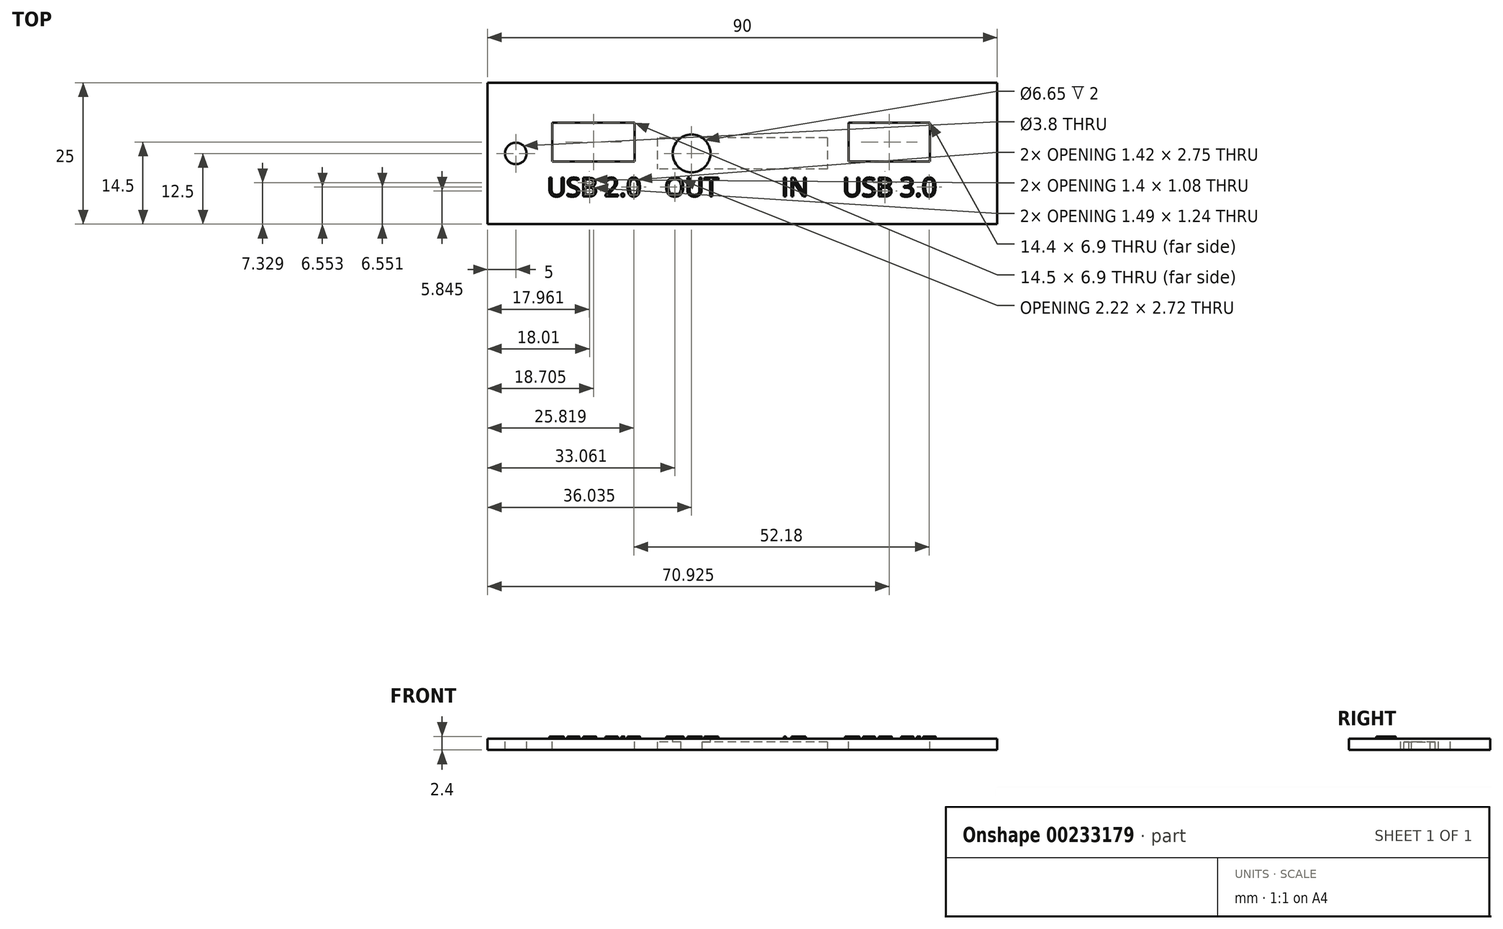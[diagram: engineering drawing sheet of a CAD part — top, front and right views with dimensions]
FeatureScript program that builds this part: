
annotation { "Feature Type Name" : "Feature", "Feature Type Description" : "" }
export const myFeature = defineFeature(function(context is Context, id is Id, definition is map)
    precondition{}
    {
        {
            var Q0;
            Q0=qCreatedBy(makeId("Top.planeOp"),FACE);
            var sketch = newSketch(context, id + "F0", { "sketchPlane" : qUnion([Q0])});
            skLineSegment(sketch, "E0.bottom", {"start": v(45, -12.5) * mm, "end": v(-45, -12.5) * mm});
            skLineSegment(sketch, "E0.top", {"start": v(45, 12.5) * mm, "end": v(-45, 12.5) * mm});
            skLineSegment(sketch, "E0.left", {"start": v(45, -12.5) * mm, "end": v(45, 12.5) * mm});
            skLineSegment(sketch, "E0.right", {"start": v(-45, -12.5) * mm, "end": v(-45, 12.5) * mm});
            skPoint(sketch, "E0.middle", {"position": v(0, 0) * mm});
            skSolve(sketch);
        }
        {
            var Q0;
            Q0=makeQuery(id+"F0.imprint","IMPRINT",FACE,{"disambiguationData":[TD([[makeQuery(id+"F0.imprint","IMPRINT",EDGE,{"derivedFrom":sQuery(id+"F0.wireOp",EDGE,"E0.bottom")}),-1.0]])]});
            extrude(context, id + "F1", {"entities" : qUnion([Q0]), "depth" : 2 * mm});
        }
        {
            var Q0;
            Q0=makeQuery(id+"F1.opExtrude","CAP_FACE",FACE,{"disambiguationData":[OSD([sQuery(id+"F0.wireOp",EDGE,"E0.bottom"),sQuery(id+"F0.wireOp",EDGE,"E0.top"),sQuery(id+"F0.wireOp",EDGE,"E0.left"),sQuery(id+"F0.wireOp",EDGE,"E0.right")])],"isStart":false});
            var sketch = newSketch(context, id + "F2", { "sketchPlane" : qUnion([Q0])});
            skCircle(sketch, "E1", {"center": v(-8.96, 0) * mm, "radius": 3.33 * mm});
            skSolve(sketch);
        }
        {
            var Q0;
            Q0=makeQuery(id+"F2.imprint","IMPRINT",FACE,{"disambiguationData":[TD([[makeQuery(id+"F2.imprint","IMPRINT",EDGE,{"derivedFrom":sQuery(id+"F2.wireOp",EDGE,"E1")}),1.0]])]});
            extrude(context, id + "F3", {"entities" : qUnion([Q0]), "operationType" : NewBodyOperationType.REMOVE, "endBound" : BoundingType.THROUGH_ALL, "oppositeDirection" : true, "depth" : 25.4 * mm});
        }
        {
            var Q0;
            Q0=makeQuery(id+"F1.opExtrude","CAP_FACE",FACE,{"disambiguationData":[OSD([sQuery(id+"F0.wireOp",EDGE,"E0.bottom"),sQuery(id+"F0.wireOp",EDGE,"E0.top"),sQuery(id+"F0.wireOp",EDGE,"E0.left"),sQuery(id+"F0.wireOp",EDGE,"E0.right")])],"isStart":false});
            var sketch = newSketch(context, id + "F4", { "sketchPlane" : qUnion([Q0])});
            skLineSegment(sketch, "E2.bottom", {"start": v(33.12, -1.45) * mm, "end": v(18.73, -1.45) * mm});
            skLineSegment(sketch, "E2.top", {"start": v(33.12, 5.45) * mm, "end": v(18.73, 5.45) * mm});
            skLineSegment(sketch, "E2.left", {"start": v(33.12, -1.45) * mm, "end": v(33.12, 5.45) * mm});
            skLineSegment(sketch, "E2.right", {"start": v(18.73, -1.45) * mm, "end": v(18.73, 5.45) * mm});
            skPoint(sketch, "E2.middle", {"position": v(25.93, 2) * mm});
            skPoint(sketch, "E3", {"position": v(8.96, 0) * mm});
            skSolve(sketch);
        }
        {
            var Q0;
            Q0=makeQuery(id+"F4.imprint","IMPRINT",FACE,{"disambiguationData":[TD([[makeQuery(id+"F4.imprint","IMPRINT",EDGE,{"derivedFrom":sQuery(id+"F4.wireOp",EDGE,"E2.bottom")}),-1.0]])]});
            extrude(context, id + "F5", {"entities" : qUnion([Q0]), "operationType" : NewBodyOperationType.REMOVE, "endBound" : BoundingType.THROUGH_ALL, "oppositeDirection" : true, "depth" : 25.4 * mm});
        }
        {
            var Q0;
            Q0=makeQuery(id+"F1.opExtrude","CAP_FACE",FACE,{"disambiguationData":[OSD([sQuery(id+"F0.wireOp",EDGE,"E0.bottom"),sQuery(id+"F0.wireOp",EDGE,"E0.top"),sQuery(id+"F0.wireOp",EDGE,"E0.left"),sQuery(id+"F0.wireOp",EDGE,"E0.right")])],"isStart":false});
            var sketch = newSketch(context, id + "F6", { "sketchPlane" : qUnion([Q0])});
            skLineSegment(sketch, "E4.bottom", {"start": v(-19.04, -1.45) * mm, "end": v(-33.55, -1.45) * mm});
            skLineSegment(sketch, "E4.top", {"start": v(-19.04, 5.45) * mm, "end": v(-33.55, 5.45) * mm});
            skLineSegment(sketch, "E4.left", {"start": v(-19.04, -1.45) * mm, "end": v(-19.04, 5.45) * mm});
            skLineSegment(sketch, "E4.right", {"start": v(-33.55, -1.45) * mm, "end": v(-33.55, 5.45) * mm});
            skPoint(sketch, "E4.middle", {"position": v(-26.3, 2) * mm});
            skPoint(sketch, "E5", {"position": v(-8.96, 0) * mm});
            skLineSegment(sketch, "E6.bottom", {"start": v(15, 2.75) * mm, "end": v(-15, 2.75) * mm});
            skLineSegment(sketch, "E6.top", {"start": v(15, -2.75) * mm, "end": v(-15, -2.75) * mm});
            skLineSegment(sketch, "E6.left", {"start": v(15, 2.75) * mm, "end": v(15, -2.75) * mm});
            skLineSegment(sketch, "E6.right", {"start": v(-15, 2.75) * mm, "end": v(-15, -2.75) * mm});
            skPoint(sketch, "E6.middle", {"position": v(0, 0) * mm});
            skSolve(sketch);
        }
        {
            var Q0;
            Q0=makeQuery(id+"F6.imprint","IMPRINT",FACE,{"disambiguationData":[TD([[makeQuery(id+"F6.imprint","IMPRINT",EDGE,{"derivedFrom":sQuery(id+"F6.wireOp",EDGE,"E4.bottom")}),-1.0]])]});
            extrude(context, id + "F7", {"entities" : qUnion([Q0]), "operationType" : NewBodyOperationType.REMOVE, "endBound" : BoundingType.THROUGH_ALL, "oppositeDirection" : true, "depth" : 25.4 * mm});
        }
        {
            var Q0;
            Q0=makeQuery(id+"F1.opExtrude","CAP_FACE",FACE,{"disambiguationData":[OSD([sQuery(id+"F0.wireOp",EDGE,"E0.bottom"),sQuery(id+"F0.wireOp",EDGE,"E0.top"),sQuery(id+"F0.wireOp",EDGE,"E0.left"),sQuery(id+"F0.wireOp",EDGE,"E0.right")])],"isStart":false});
            var sketch = newSketch(context, id + "F8", { "sketchPlane" : qUnion([Q0])});
            skLineSegment(sketch, "E7.0", {"start": v(-18.04, 6.45) * mm, "end": v(-34.55, 6.45) * mm});
            skLineSegment(sketch, "E7.1", {"start": v(-18.05, -2.45) * mm, "end": v(-18.04, 6.45) * mm});
            skLineSegment(sketch, "E7.2", {"start": v(-18.05, -2.45) * mm, "end": v(-34.55, -2.45) * mm});
            skLineSegment(sketch, "E7.3", {"start": v(-34.55, -2.45) * mm, "end": v(-34.55, 6.45) * mm});
            skLineSegment(sketch, "E8.0", {"start": v(51.35, -18.85) * mm, "end": v(51.35, 18.85) * mm});
            skLineSegment(sketch, "E8.1", {"start": v(-51.35, -18.85) * mm, "end": v(51.35, -18.85) * mm});
            skLineSegment(sketch, "E8.2", {"start": v(-51.35, 18.85) * mm, "end": v(-51.35, -18.85) * mm});
            skLineSegment(sketch, "E8.3", {"start": v(51.35, 18.85) * mm, "end": v(-51.35, 18.85) * mm});
            skSolve(sketch);
        }
        {
            var Q0;
            Q0=makeQuery(id+"F1.opExtrude","CAP_FACE",FACE,{"disambiguationData":[OSD([sQuery(id+"F0.wireOp",EDGE,"E0.bottom"),sQuery(id+"F0.wireOp",EDGE,"E0.top"),sQuery(id+"F0.wireOp",EDGE,"E0.left"),sQuery(id+"F0.wireOp",EDGE,"E0.right")])],"isStart":false});
            var sketch = newSketch(context, id + "F9", { "sketchPlane" : qUnion([Q0])});
            skLineSegment(sketch, "E9.0", {"start": v(34.12, 6.45) * mm, "end": v(17.73, 6.45) * mm});
            skLineSegment(sketch, "E9.1", {"start": v(34.12, -2.45) * mm, "end": v(34.12, 6.45) * mm});
            skLineSegment(sketch, "E9.2", {"start": v(34.12, -2.45) * mm, "end": v(17.73, -2.45) * mm});
            skLineSegment(sketch, "E9.3", {"start": v(17.73, -2.45) * mm, "end": v(17.73, 6.45) * mm});
            skLineSegment(sketch, "E10.0", {"start": v(51.35, -18.85) * mm, "end": v(51.35, 18.85) * mm});
            skLineSegment(sketch, "E10.1", {"start": v(-51.35, -18.85) * mm, "end": v(51.35, -18.85) * mm});
            skLineSegment(sketch, "E10.2", {"start": v(-51.35, 18.85) * mm, "end": v(-51.35, -18.85) * mm});
            skLineSegment(sketch, "E10.3", {"start": v(51.35, 18.85) * mm, "end": v(-51.35, 18.85) * mm});
            skSolve(sketch);
        }
        {
            var Q0;
            Q0=makeQuery(id+"F8.imprint","IMPRINT",FACE,{"disambiguationData":[TD([[makeQuery(id+"F8.imprint","IMPRINT",EDGE,{"derivedFrom":sQuery(id+"F8.wireOp",EDGE,"E7.0")}),-1.0]])]});
            var sketch = newSketch(context, id + "F10", { "sketchPlane" : qUnion([Q0])});
            skText(sketch, "E11", { "text": "USB 2.0", "fontName": "OpenSans-Regular.ttf"});
            skText(sketch, "E12", { "text": "OUT", "fontName": "OpenSans-Regular.ttf"});
            skText(sketch, "E13", { "text": "IN", "fontName": "OpenSans-Regular.ttf"});
            skText(sketch, "E14", { "text": "USB 3.0", "fontName": "OpenSans-Regular.ttf"});
            const initialGuessF10  = {"E11": [-0.03448, -0.0076, 1, 0, 0.00333], "E12": [-0.01374, -0.0076, 1, 0, 0.00333], "E13": [0.0069, -0.0076, 1, 0, 0.00333], "E14": [0.0177, -0.0076, 1, 0, 0.00333]};
            skSetInitialGuess(sketch, initialGuessF10);
            skSolve(sketch);
        }
        {
            var Q0;
            Q0 = qSketchRegion(id + "F10", true);
            extrude(context, id + "F11", {"entities" : qUnion([Q0]), "depth" : .4 * mm});
        }
        {
            var Q0;
            Q0=makeQuery(id+"F8.imprint","IMPRINT",FACE,{"disambiguationData":[TD([[makeQuery(id+"F8.imprint","IMPRINT",EDGE,{"derivedFrom":sQuery(id+"F8.wireOp",EDGE,"E7.0")}),-1.0]])]});
            var sketch = newSketch(context, id + "F12", { "sketchPlane" : qUnion([Q0])});
            skPoint(sketch, "E15", {"position": v(-40, 0) * mm});
            skSolve(sketch);
        }
        {
            var Q0;
            Q0=sQuery(id+"F12.wireOp",VERTEX,"E15");
            var Q1;
            Q1=makeQuery(id+"F1.opExtrude","SWEPT_BODY",BODY,{"disambiguationData":[OSD([sQuery(id+"F0.wireOp",EDGE,"E0.bottom"),sQuery(id+"F0.wireOp",EDGE,"E0.top"),sQuery(id+"F0.wireOp",EDGE,"E0.left"),sQuery(id+"F0.wireOp",EDGE,"E0.right")])]});
            hole(context, id + "F13", {"style" : HoleStyle.SIMPLE, "endStyle" : HoleEndStyle.THROUGH, "standardTappedOrClearance" : lookupTablePath({ "standard" : "ANSI", "fit" : "Normal (ASME)", "size" : "#6", "type" : "Clearance" }), "standardBlindInLast" : lookupTablePath({ "fit" : "Free", "standard" : "ANSI", "size" : "#6", "type" : "Clearance" }), "holeDiameter" : 3.8 * mm, "locations" : qUnion([Q0]), "scope" : qUnion([Q1]), "isTappedThrough" : true});
        }
        {
            var Q0;
            Q0=makeQuery(id+"F1.opExtrude","CAP_FACE",FACE,{"disambiguationData":[OSD([sQuery(id+"F0.wireOp",EDGE,"E0.bottom"),sQuery(id+"F0.wireOp",EDGE,"E0.top"),sQuery(id+"F0.wireOp",EDGE,"E0.left"),sQuery(id+"F0.wireOp",EDGE,"E0.right")])],"isStart":true});
            var sketch = newSketch(context, id + "F14", { "sketchPlane" : qUnion([Q0])});
            skLineSegment(sketch, "E16.bottom", {"start": v(15, -2.75) * mm, "end": v(-15, -2.75) * mm});
            skLineSegment(sketch, "E16.top", {"start": v(15, 2.75) * mm, "end": v(-15, 2.75) * mm});
            skLineSegment(sketch, "E16.left", {"start": v(15, -2.75) * mm, "end": v(15, 2.75) * mm});
            skLineSegment(sketch, "E16.right", {"start": v(-15, -2.75) * mm, "end": v(-15, 2.75) * mm});
            skPoint(sketch, "E16.middle", {"position": v(0, 0) * mm});
            skSolve(sketch);
        }
        {
            var Q0;
            Q0 = qSketchRegion(id + "F14", true);
            extrude(context, id + "F15", {"entities" : qUnion([Q0]), "operationType" : NewBodyOperationType.REMOVE, "oppositeDirection" : true, "depth" : 1.4 * mm});
        }
    });
